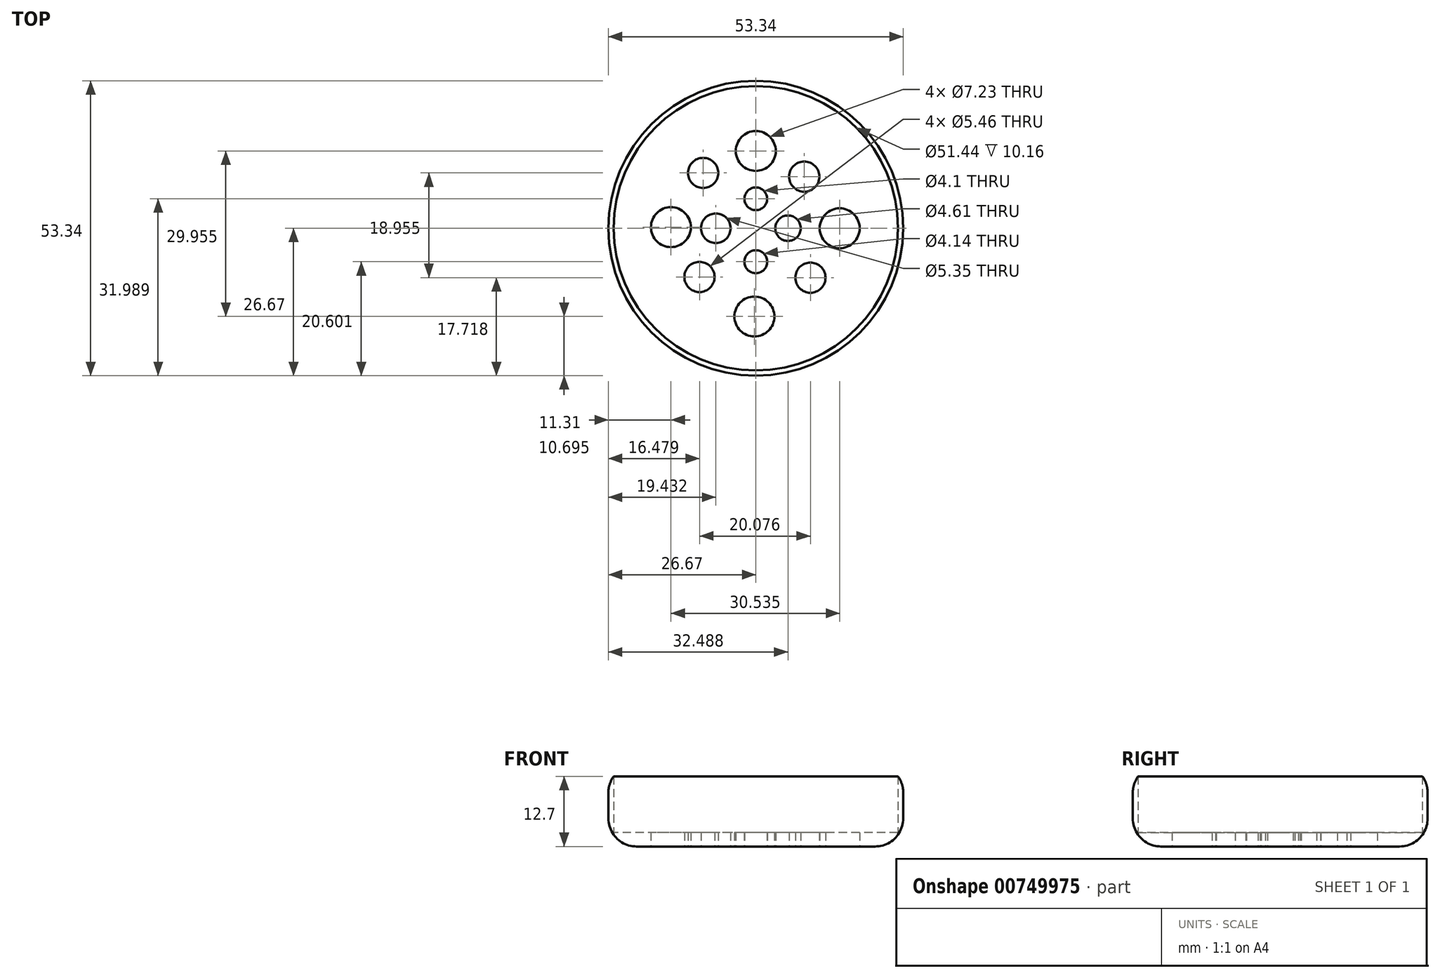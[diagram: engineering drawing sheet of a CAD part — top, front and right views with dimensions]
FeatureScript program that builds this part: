
annotation { "Feature Type Name" : "Feature", "Feature Type Description" : "" }
export const myFeature = defineFeature(function(context is Context, id is Id, definition is map)
    precondition{}
    {
        {
            var Q0;
            Q0=qCreatedBy(makeId("Top.planeOp"),FACE);
            var sketch = newSketch(context, id + "F0", { "sketchPlane" : qUnion([Q0])});
            skCircle(sketch, "E0", {"center": v(0, 0) * mm, "radius": 25.72 * mm});
            skCircle(sketch, "E1", {"center": v(0, 0) * mm, "radius": 26.67 * mm});
            skCircle(sketch, "E2", {"center": v(0, 13.98) * mm, "radius": 3.61 * mm});
            skCircle(sketch, "E3", {"center": v(-15.36, 0.2) * mm, "radius": 3.61 * mm});
            skCircle(sketch, "E4", {"center": v(-0.25, -15.98) * mm, "radius": 3.61 * mm});
            skCircle(sketch, "E5", {"center": v(8.76, 9.34) * mm, "radius": 2.73 * mm});
            skCircle(sketch, "E6", {"center": v(-9.53, 10) * mm, "radius": 2.73 * mm});
            skCircle(sketch, "E7", {"center": v(-10.2, -8.82) * mm, "radius": 2.73 * mm});
            skCircle(sketch, "E8.MirrorC", {"center": v(9.89, -8.95) * mm, "radius": 2.73 * mm});
            skCircle(sketch, "E9.MirrorC", {"center": v(15.17, 0) * mm, "radius": 3.61 * mm});
            skCircle(sketch, "E10", {"center": v(-7.24, 0) * mm, "radius": 2.68 * mm});
            skCircle(sketch, "E11", {"center": v(0, -6.07) * mm, "radius": 2.07 * mm});
            skCircle(sketch, "E12", {"center": v(5.82, 0) * mm, "radius": 2.3 * mm});
            skCircle(sketch, "E13", {"center": v(0, 5.32) * mm, "radius": 2.05 * mm});
            skSolve(sketch);
        }
        {
            var Q0;
            Q0 = qSketchRegion(id + "F0", true);
            extrude(context, id + "F1", {"entities" : qUnion([Q0]), "depth" : 12.7 * mm, "offsetDistance" : 25.4 * mm});
        }
        {
            var Q0;
            Q0=makeQuery(id+"F0.imprint","IMPRINT",FACE,{"disambiguationData":[TD([[makeQuery(id+"F0.imprint","IMPRINT",EDGE,{"derivedFrom":sQuery(id+"F0.wireOp",EDGE,"E0")}),1.0]])]});
            extrude(context, id + "F2", {"entities" : qUnion([Q0]), "operationType" : NewBodyOperationType.ADD, "depth" : 2.54 * mm, "offsetDistance" : 25.4 * mm});
        }
        {
            var Q0;
            Q0=makeQuery(id+"F1.opExtrude","CAP_EDGE",EDGE,{"disambiguationData":[OSD([sQuery(id+"F0.wireOp",EDGE,"E1")])],"isStart":true});
            fillet(context, id + "F3", {"entities" : qUnion([Q0]), "radius" : 5.08 * mm, "tangentPropagation" : true, "allowEdgeOverflow" : false});
        }
        {
            var Q0;
            Q0=makeQuery(id+"F1.opExtrude","CAP_EDGE",EDGE,{"disambiguationData":[OSD([sQuery(id+"F0.wireOp",EDGE,"E1")])],"isStart":false});
            fillet(context, id + "F4", {"entities" : qUnion([Q0]), "radius" : 5.08 * mm, "tangentPropagation" : true, "allowEdgeOverflow" : false});
        }
    });
